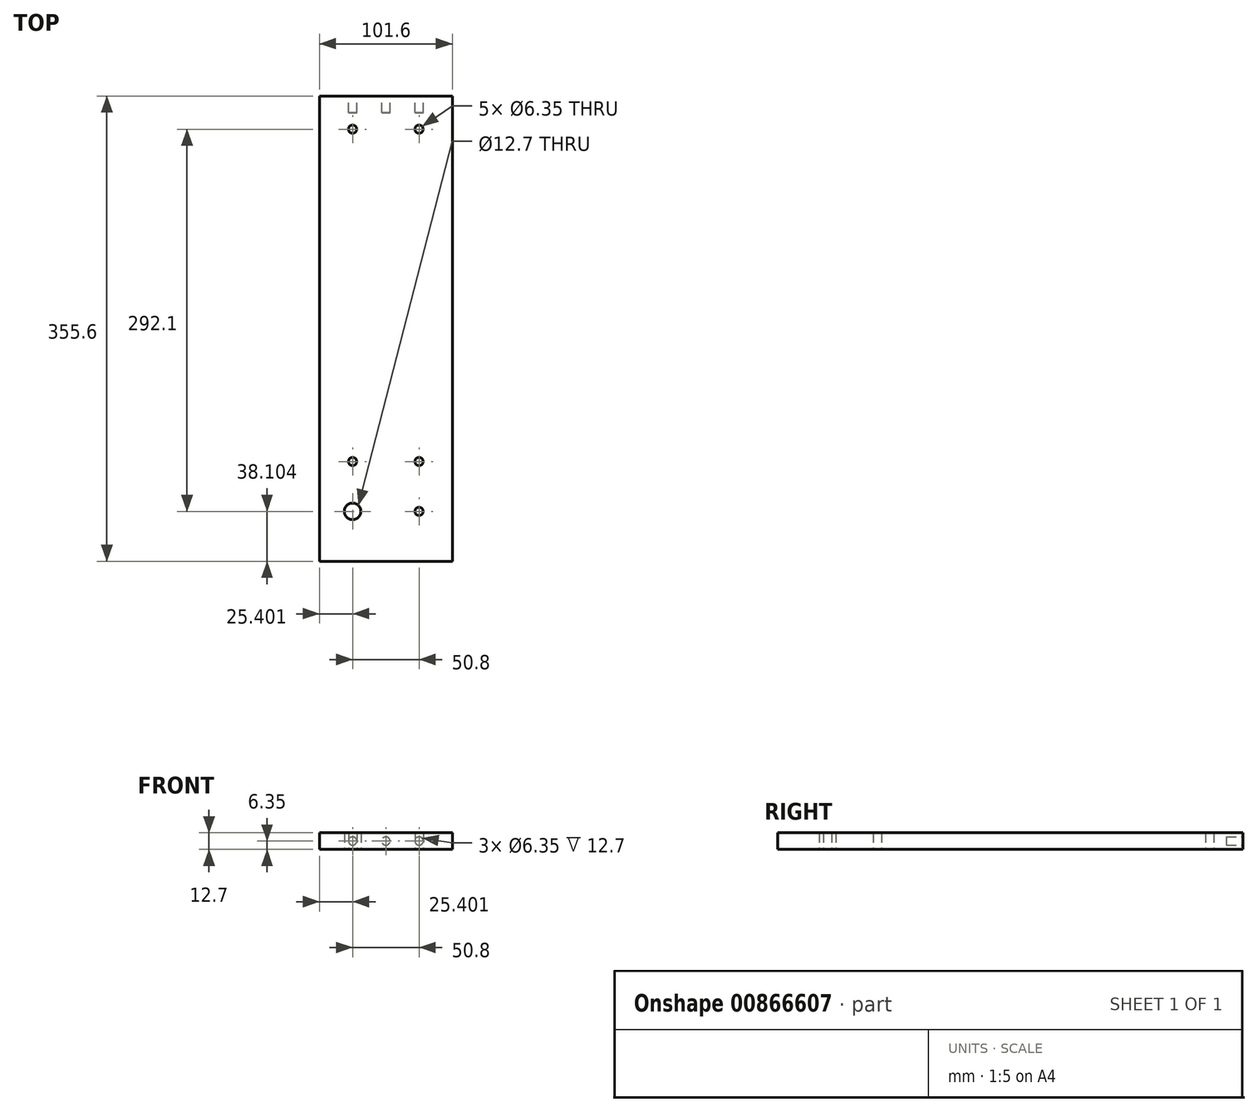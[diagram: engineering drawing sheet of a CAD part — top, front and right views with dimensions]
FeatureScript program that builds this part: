
annotation { "Feature Type Name" : "Feature", "Feature Type Description" : "" }
export const myFeature = defineFeature(function(context is Context, id is Id, definition is map)
    precondition{}
    {
        {
            var Q0;
            Q0=qCreatedBy(makeId("Top.planeOp"),FACE);
            var sketch = newSketch(context, id + "F0", { "sketchPlane" : qUnion([Q0])});
            skLineSegment(sketch, "E0.bottom", {"start": v(-48.44, 280.45) * mm, "end": v(53.16, 280.45) * mm});
            skLineSegment(sketch, "E0.top", {"start": v(-48.44, -75.15) * mm, "end": v(53.16, -75.15) * mm});
            skLineSegment(sketch, "E0.left", {"start": v(-48.44, 280.45) * mm, "end": v(-48.44, -75.15) * mm});
            skLineSegment(sketch, "E0.right", {"start": v(53.16, 280.45) * mm, "end": v(53.16, -75.15) * mm});
            skCircle(sketch, "E1", {"center": v(-23.04, 255.05) * mm, "radius": 3.18 * mm});
            skCircle(sketch, "E2", {"center": v(27.76, 255.05) * mm, "radius": 3.18 * mm});
            skCircle(sketch, "E3", {"center": v(-23.04, 1.05) * mm, "radius": 3.18 * mm});
            skCircle(sketch, "E4", {"center": v(27.76, 1.05) * mm, "radius": 3.18 * mm});
            skCircle(sketch, "E5", {"center": v(-23.04, -37.05) * mm, "radius": 6.35 * mm});
            skCircle(sketch, "E6", {"center": v(27.76, -37.05) * mm, "radius": 3.18 * mm});
            skSolve(sketch);
        }
        {
            var Q0;
            Q0=makeQuery(id+"F0.imprint","IMPRINT",FACE,{"disambiguationData":[TD([[makeQuery(id+"F0.imprint","IMPRINT",EDGE,{"derivedFrom":sQuery(id+"F0.wireOp",EDGE,"E0.bottom")}),-1.0]])]});
            extrude(context, id + "F1", {"entities" : qUnion([Q0]), "depth" : 12.7 * mm, "offsetDistance" : 25.4 * mm});
        }
        {
            var Q0;
            Q0=makeQuery(id+"F1.opExtrude","SWEPT_FACE",FACE,{"disambiguationData":[OSD([sQuery(id+"F0.wireOp",EDGE,"E0.bottom")])]});
            var sketch = newSketch(context, id + "F2", { "sketchPlane" : qUnion([Q0])});
            skCircle(sketch, "E7", {"center": v(-27.76, 6.35) * mm, "radius": 3.18 * mm});
            skCircle(sketch, "E8", {"center": v(-2.36, 6.35) * mm, "radius": 3.18 * mm});
            skCircle(sketch, "E9", {"center": v(23.04, 6.35) * mm, "radius": 3.18 * mm});
            skSolve(sketch);
        }
        {
            var Q0;
            Q0=makeQuery(id+"F2.imprint","IMPRINT",FACE,{"disambiguationData":[TD([[makeQuery(id+"F2.imprint","IMPRINT",EDGE,{"derivedFrom":sQuery(id+"F2.wireOp",EDGE,"E7")}),1.0]])]});
            var Q1;
            Q1=makeQuery(id+"F2.imprint","IMPRINT",FACE,{"disambiguationData":[TD([[makeQuery(id+"F2.imprint","IMPRINT",EDGE,{"derivedFrom":sQuery(id+"F2.wireOp",EDGE,"E8")}),1.0]])]});
            var Q2;
            Q2=makeQuery(id+"F2.imprint","IMPRINT",FACE,{"disambiguationData":[TD([[makeQuery(id+"F2.imprint","IMPRINT",EDGE,{"derivedFrom":sQuery(id+"F2.wireOp",EDGE,"E9")}),1.0]])]});
            extrude(context, id + "F3", {"entities" : qUnion([Q0, Q1, Q2]), "operationType" : NewBodyOperationType.REMOVE, "oppositeDirection" : true, "depth" : 12.7 * mm, "offsetDistance" : 25.4 * mm});
        }
    });
